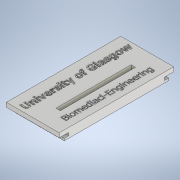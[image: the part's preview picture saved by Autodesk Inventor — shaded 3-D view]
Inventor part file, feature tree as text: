
AUTODESK INVENTOR PART (.ipt)
format: ipt  version: 2021 (Build 250183000, 183)  size: 1,300,480 bytes
history: native  units: mm
features: sketch x9, extrude x8, other x1
ambient origin geometry x8: Origin, YZ Plane, XZ Plane, XY Plane, X Axis, Y Axis, Z Axis, Center Point
bodies: 实体1 (feature_tree)
feature tree (18):
  extrude  "拉伸1"  Depth=37.0mm
  extrude  "拉伸2"  Depth=6.5mm
  extrude  "拉伸3"  Depth=2.0mm
  extrude  "拉伸4"  Depth=1.0mm
  extrude  "拉伸6"  Depth=80.0mm TaperAngle=0.0deg
  extrude  "拉伸7"  Depth=80.0mm TaperAngle=0.0deg
  extrude  "拉伸8"  Depth=3.5mm
  extrude  "拉伸5"  Depth=21.0mm
  other  "凸雕3"
  sketch  "草图1"  dims[d0=80.0mm d1=37.0mm]
  sketch  "草图2"  dims[d2=4.0mm d3=0.0mm d4=6.5mm]
  sketch  "草图3"  dims[d5=1.0mm d6=2.0mm]
  sketch  "草图4"  dims[d7=6.5mm d8=1.0mm]
  sketch  "草图5"  dims[d9=2.0mm d10=80.0mm d11=0.0mm]
  sketch  "草图8"  dims[d12=5.5mm d13=80.0mm d14=0.0mm]
  sketch  "草图9"  dims[d15=3.5mm d16=3.5mm]
  sketch  "草图10"  dims[d17=80.0mm d18=0.0mm d19=21.0mm]
  sketch  "草图12"  dims[d20=3.0mm d21=52.5mm d22=13.75mm d23=80.0mm d24=0.0mm d29=3.0mm d30=1.0mm d31=0.0mm d32=2.0mm d33=0.0mm d34=0.6mm d35=0.0mm d36=40.0mm d37=0.0mm d38=1.0mm d39=0.0mm]
